# Revit family: Haworth_BuzziSpark_Sofa_TwoSeats_Open_EU_PRELIMINARY
name_source: partatom
category: Furniture
revit_build: Autodesk Revit 2018 (Build: 20170223_1515(x64)
units: mm (PartAtom-declared; Revit-internal decimal feet)

## family parameters
Always vertical = Yes
Cut with Voids When Loaded = No
OmniClass Number = 23.40.70.14.64.21
OmniClass Title = Systems Furniture
Room Calculation Point = No
Shared = No
Work Plane-Based = No

## types (5) — shared parameters
Actual Depth = 95 cm
Actual Width = 239 cm
Arm Offset = 14 cm
Assembly Code = E2020200
Back Cushion Offset = 50 cm
Back Cushion Width = 98 cm
Back Upholstery Width = 111 cm
Description = Haworth - BuzziSpark - Sofa - Two Seats - Open
Left tablet = Yes
Manufacturer = Haworth
Middle Leg Control = No
Model = Original AG 102
Revision Number = 1
Right Tablet = Yes
Seat Depth = 70 cm
Seat Height = 45 cm
Seat Offset = 55 cm
Seat Width = 111 cm
Shield 1 Height = Haworth_BuzziSpark_Sofa_ShieldUpholstery_Part : Medium
Shield 2 Height = Haworth_BuzziSpark_Sofa_ShieldUpholstery_Part : Medium
Shield Width = 115 cm
Shield w Tube Thickness = 9 cm
Side Upholstery Width = 65 cm
Size = Verify Final Dim. w/ Haworth
URL = https://www.haworth.com
URL - Product = https://www.haworth.com
Warranty = http://www.haworth.com
With Arm Cushion = Yes

## per-type parameters (varying)
| type | Left High Back | Left Low Back | Left Medium Back | Right High Back | Right Low Back | Right Medium Back |
| High - High | Yes | No | No | Yes | No | No |
| Low - Low | No | Yes | No | No | Yes | No |
| High - Medium | Yes | No | No | No | No | Yes |
| Medium - High | No | No | Yes | Yes | No | No |
| Medium - Medium | No | No | Yes | No | No | Yes |

## geometry (parser evidence)
native form markers: Sweep x16
no freeform markers — native parametric forms only
